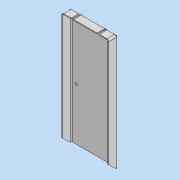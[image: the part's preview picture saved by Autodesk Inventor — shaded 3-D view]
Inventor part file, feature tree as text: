
AUTODESK INVENTOR PART (.ipt)
format: ipt  version: 2020 (Build 240168000, 168)  size: 167,936 bytes
history: native  units: mm
features: other x14, sketch x6, extrude x1, hole x1, chamfer x1
ambient origin geometry x8: Origin, YZ Plane, XZ Plane, XY Plane, X Axis, Y Axis, Z Axis, Center Point
bodies: Body1 (feature_tree)
feature tree (23):
  other  "ソリッド1"
  other  "フランジ1"
  other  "フランジ5"
  extrude  "押し出し1"  Depth=100.0mm
  other  "フランジ6"
  hole  "穴1"  [1 undecoded]
  chamfer  "面取り1"  Distance=242.0mm
  sketch  "スケッチ1"
  other  "プレート1"
  sketch  "スケッチ2"
  other  "プレート2"
  other  "曲げ1"
  other  "コーナー1"
  sketch  "スケッチ6"
  other  "プレート6"
  other  "曲げ5"
  other  "コーナー5"
  sketch  "スケッチ7"
  sketch  "スケッチ8"
  other  "プレート7"
  other  "曲げ6"
  other  "コーナー6"
  sketch  "スケッチ9"
note: 1 required parameter value undecoded (feature->parameter linkage not recoverable at this tier; creation-order binding heuristic only, values carry confidence <= 0.55)
